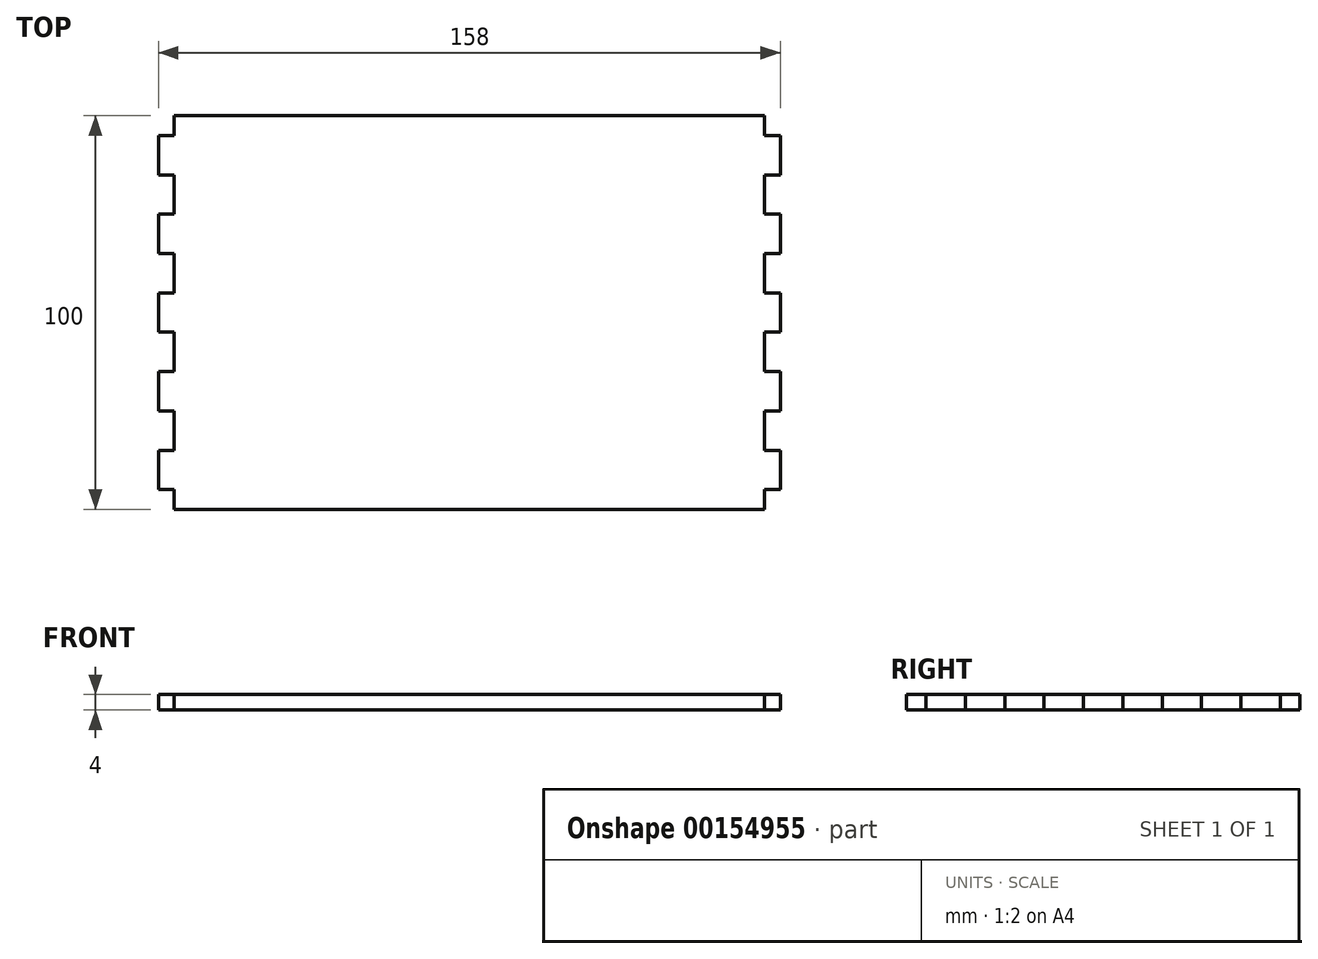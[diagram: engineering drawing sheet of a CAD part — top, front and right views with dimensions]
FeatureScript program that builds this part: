
annotation { "Feature Type Name" : "Feature", "Feature Type Description" : "" }
export const myFeature = defineFeature(function(context is Context, id is Id, definition is map)
    precondition{}
    {
        {
            var Q0;
            Q0=qCreatedBy(makeId("Top.planeOp"),FACE);
            var sketch = newSketch(context, id + "F0", { "sketchPlane" : qUnion([Q0])});
            skLineSegment(sketch, "E0.bottom", {"start": v(75, 50) * mm, "end": v(-75, 50) * mm});
            skLineSegment(sketch, "E0.top", {"start": v(75, -50) * mm, "end": v(-75, -50) * mm});
            skLineSegment(sketch, "E0.left", {"start": v(75, 50) * mm, "end": v(75, -50) * mm});
            skLineSegment(sketch, "E0.right", {"start": v(-75, 50) * mm, "end": v(-75, -50) * mm});
            skPoint(sketch, "E0.middle", {"position": v(0, 0) * mm});
            skSolve(sketch);
        }
        {
            var Q0;
            Q0 = qSketchRegion(id + "F0", true);
            extrude(context, id + "F1", {"entities" : qUnion([Q0]), "depth" : 4 * mm});
        }
        {
            var Q0;
            Q0=makeQuery(id+"F1.opExtrude","CAP_FACE",FACE,{"disambiguationData":[OSD([sQuery(id+"F0.wireOp",EDGE,"E0.bottom"),sQuery(id+"F0.wireOp",EDGE,"E0.top"),sQuery(id+"F0.wireOp",EDGE,"E0.left"),sQuery(id+"F0.wireOp",EDGE,"E0.right")])],"isStart":false});
            var sketch = newSketch(context, id + "F2", { "sketchPlane" : qUnion([Q0])});
            skLineSegment(sketch, "E1", {"start": v(-75, -50) * mm, "end": v(-75, -45) * mm});
            skLineSegment(sketch, "E2.bottom", {"start": v(-75, -45) * mm, "end": v(-79, -45) * mm});
            skLineSegment(sketch, "E2.top", {"start": v(-75, -35) * mm, "end": v(-79, -35) * mm});
            skLineSegment(sketch, "E2.left", {"start": v(-75, -45) * mm, "end": v(-75, -35) * mm});
            skLineSegment(sketch, "E2.right", {"start": v(-79, -45) * mm, "end": v(-79, -35) * mm});
            skLineSegment(sketch, "E3.0.1.0", {"start": v(-75, -25) * mm, "end": v(-79, -25) * mm});
            skLineSegment(sketch, "E3.0.1.1", {"start": v(-75, -15) * mm, "end": v(-79, -15) * mm});
            skLineSegment(sketch, "E3.0.1.2", {"start": v(-75, -25) * mm, "end": v(-75, -15) * mm});
            skLineSegment(sketch, "E3.0.1.3", {"start": v(-79, -25) * mm, "end": v(-79, -15) * mm});
            skLineSegment(sketch, "E3.0.2.0", {"start": v(-75, -5) * mm, "end": v(-79, -5) * mm});
            skLineSegment(sketch, "E3.0.2.1", {"start": v(-75, 5) * mm, "end": v(-79, 5) * mm});
            skLineSegment(sketch, "E3.0.2.2", {"start": v(-75, -5) * mm, "end": v(-75, 5) * mm});
            skLineSegment(sketch, "E3.0.2.3", {"start": v(-79, -5) * mm, "end": v(-79, 5) * mm});
            skLineSegment(sketch, "E3.0.3.0", {"start": v(-75, 15) * mm, "end": v(-79, 15) * mm});
            skLineSegment(sketch, "E3.0.3.1", {"start": v(-75, 25) * mm, "end": v(-79, 25) * mm});
            skLineSegment(sketch, "E3.0.3.2", {"start": v(-75, 15) * mm, "end": v(-75, 25) * mm});
            skLineSegment(sketch, "E3.0.3.3", {"start": v(-79, 15) * mm, "end": v(-79, 25) * mm});
            skLineSegment(sketch, "E3.0.4.0", {"start": v(-75, 35) * mm, "end": v(-79, 35) * mm});
            skLineSegment(sketch, "E3.0.4.1", {"start": v(-75, 45) * mm, "end": v(-79, 45) * mm});
            skLineSegment(sketch, "E3.0.4.2", {"start": v(-75, 35) * mm, "end": v(-75, 45) * mm});
            skLineSegment(sketch, "E3.0.4.3", {"start": v(-79, 35) * mm, "end": v(-79, 45) * mm});
            skLineSegment(sketch, "E3.direction1", {"start": v(-79, -45) * mm, "end": v(-54, -45) * mm, "construction": true});
            skLineSegment(sketch, "E3.direction2", {"start": v(-79, -45) * mm, "end": v(-79, -25) * mm, "construction": true});
            skLineSegment(sketch, "E4", {"start": v(0, 50) * mm, "end": v(0, 42.45) * mm});
            skLineSegment(sketch, "E5.MirrorCS", {"start": v(79, -45) * mm, "end": v(79, -35) * mm});
            skLineSegment(sketch, "E6.MirrorCS", {"start": v(75, -15) * mm, "end": v(79, -15) * mm});
            skLineSegment(sketch, "E7.MirrorCS", {"start": v(75, -25) * mm, "end": v(75, -15) * mm});
            skLineSegment(sketch, "E8.MirrorCS", {"start": v(79, -25) * mm, "end": v(79, -15) * mm});
            skLineSegment(sketch, "E9.MirrorCS", {"start": v(75, -5) * mm, "end": v(79, -5) * mm});
            skLineSegment(sketch, "E10.MirrorCS", {"start": v(75, 5) * mm, "end": v(79, 5) * mm});
            skLineSegment(sketch, "E11.MirrorCS", {"start": v(75, -5) * mm, "end": v(75, 5) * mm});
            skLineSegment(sketch, "E12.MirrorCS", {"start": v(79, -5) * mm, "end": v(79, 5) * mm});
            skLineSegment(sketch, "E13.MirrorCS", {"start": v(79, -45) * mm, "end": v(79, -25) * mm, "construction": true});
            skLineSegment(sketch, "E14.MirrorCS", {"start": v(79, 35) * mm, "end": v(79, 45) * mm});
            skLineSegment(sketch, "E15.MirrorCS", {"start": v(75, 45) * mm, "end": v(79, 45) * mm});
            skLineSegment(sketch, "E16.MirrorCS", {"start": v(79, 15) * mm, "end": v(79, 25) * mm});
            skLineSegment(sketch, "E17.MirrorCS", {"start": v(75, 35) * mm, "end": v(75, 45) * mm});
            skLineSegment(sketch, "E18.MirrorCS", {"start": v(75, 35) * mm, "end": v(79, 35) * mm});
            skLineSegment(sketch, "E19.MirrorCS", {"start": v(75, 15) * mm, "end": v(79, 15) * mm});
            skLineSegment(sketch, "E20.MirrorCS", {"start": v(75, -25) * mm, "end": v(79, -25) * mm});
            skLineSegment(sketch, "E21.MirrorCS", {"start": v(75, -45) * mm, "end": v(75, -35) * mm});
            skLineSegment(sketch, "E22.MirrorCS", {"start": v(75, -35) * mm, "end": v(79, -35) * mm});
            skLineSegment(sketch, "E23.MirrorCS", {"start": v(75, -45) * mm, "end": v(79, -45) * mm});
            skLineSegment(sketch, "E24.MirrorCS", {"start": v(75, -50) * mm, "end": v(75, -45) * mm});
            skLineSegment(sketch, "E25.MirrorCS", {"start": v(75, 15) * mm, "end": v(75, 25) * mm});
            skLineSegment(sketch, "E26.MirrorCS", {"start": v(75, 25) * mm, "end": v(79, 25) * mm});
            skSolve(sketch);
        }
        {
            var Q0;
            Q0 = qSketchRegion(id + "F2", true);
            extrude(context, id + "F3", {"entities" : qUnion([Q0]), "operationType" : NewBodyOperationType.ADD, "oppositeDirection" : true, "depth" : 4 * mm});
        }
    });
